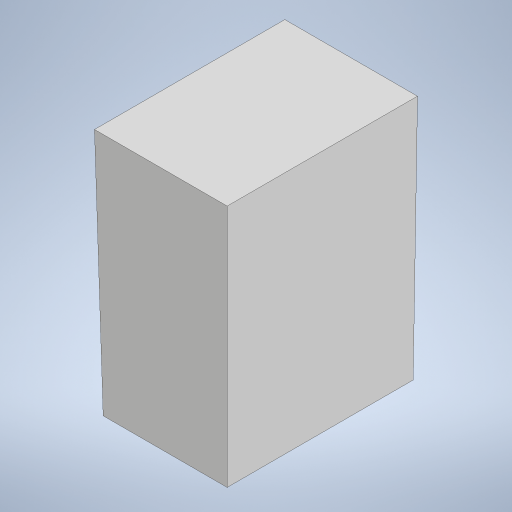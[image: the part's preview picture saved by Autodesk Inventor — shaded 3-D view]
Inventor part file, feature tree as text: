
AUTODESK INVENTOR PART (.ipt)
format: ipt  version: 2023 (Build 270158000, 158)  size: 197,120 bytes
history: native  units: in
note: dims shown in document units (in); Inventor stores cm internally (conversion verified against a paired STEP export)
features: extrude x2, sketch x1, draft x1
ambient origin geometry x8: Origin, YZ Plane, XZ Plane, XY Plane, X Axis, Y Axis, Z Axis, Center Point
bodies: Solid1 (feature_tree)
feature tree (4):
  sketch  "Sketch1"  dims[d0=0.5in d1=1.0in d2=1.5in d3=0.5in d4=0.5in d5=2.0in d6=0.0in d7=1.75in d8=0.0in d20=0.0069in]
  extrude  "Extrusion1"  Depth=0.0069in
  extrude  "Extrusion2"  Depth=0.0069in
  draft  "FaceDraft1"
